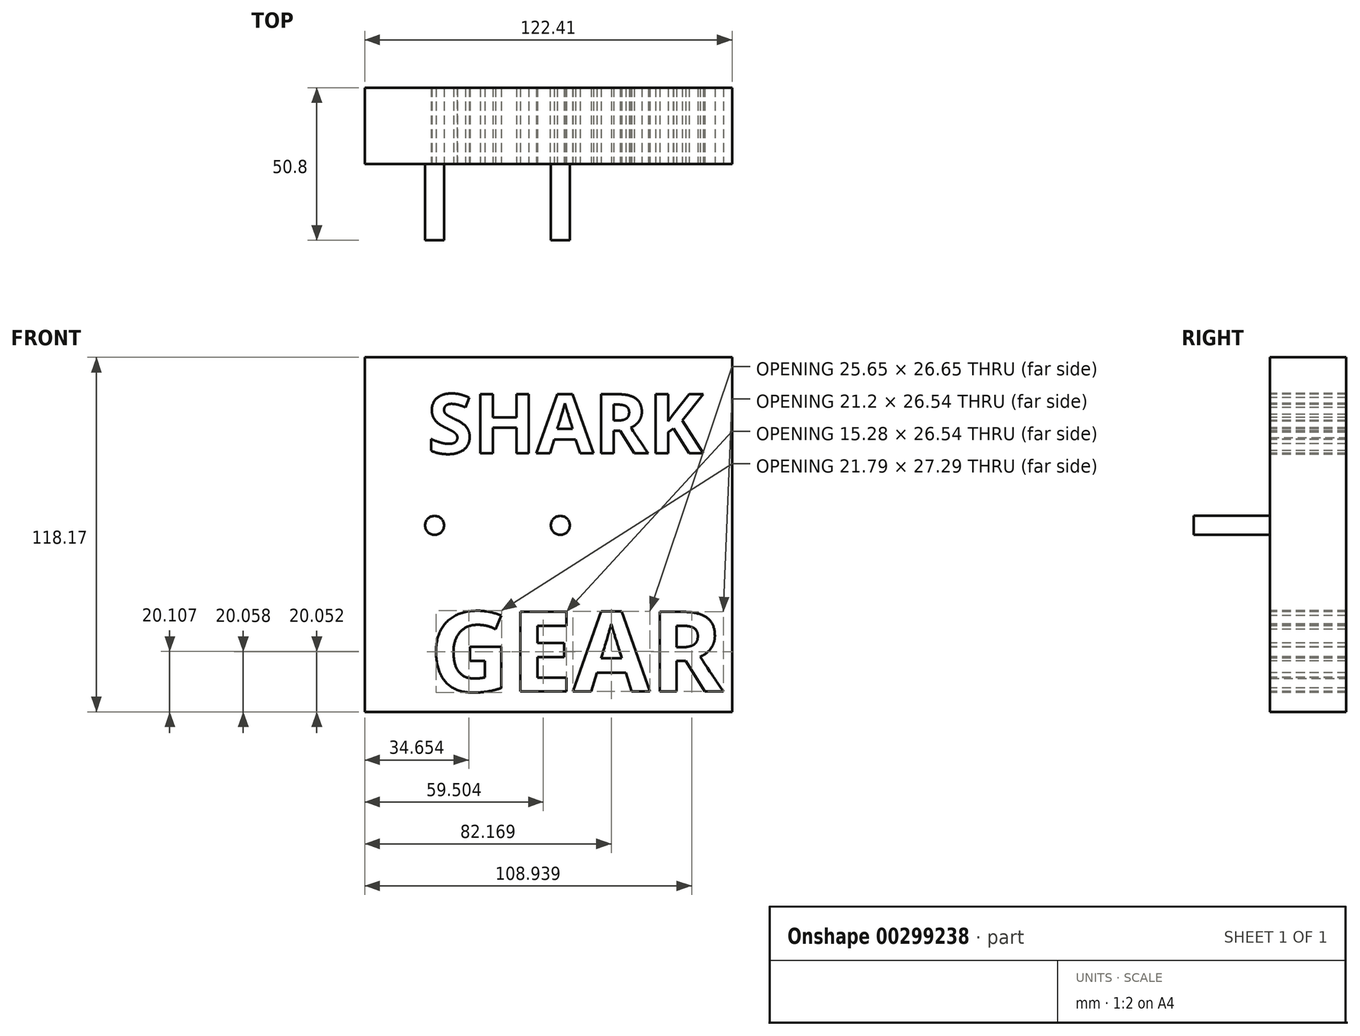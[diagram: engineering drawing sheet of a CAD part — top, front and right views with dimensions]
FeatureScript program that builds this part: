
annotation { "Feature Type Name" : "Feature", "Feature Type Description" : "" }
export const myFeature = defineFeature(function(context is Context, id is Id, definition is map)
    precondition{}
    {
        {
            var Q0;
            Q0=qCreatedBy(makeId("Front.planeOp"),FACE);
            var sketch = newSketch(context, id + "F0", { "sketchPlane" : qUnion([Q0])});
            skLineSegment(sketch, "E0.bottom", {"start": v(-56.78, 56.04) * mm, "end": v(65.63, 56.04) * mm});
            skLineSegment(sketch, "E0.top", {"start": v(-56.78, -62.13) * mm, "end": v(65.63, -62.13) * mm});
            skLineSegment(sketch, "E0.left", {"start": v(-56.78, 56.04) * mm, "end": v(-56.78, -62.13) * mm});
            skLineSegment(sketch, "E0.right", {"start": v(65.63, 56.04) * mm, "end": v(65.63, -62.13) * mm});
            skSolve(sketch);
        }
        {
            var Q0;
            Q0=makeQuery(id+"F0.imprint","IMPRINT",FACE,{"disambiguationData":[TD([[makeQuery(id+"F0.imprint","IMPRINT",EDGE,{"derivedFrom":sQuery(id+"F0.wireOp",EDGE,"E0.bottom")}),-1.0]])]});
            var sketch = newSketch(context, id + "F1", { "sketchPlane" : qUnion([Q0])});
            skCircle(sketch, "E1", {"center": v(-33.52, 0) * mm, "radius": 3.18 * mm});
            skCircle(sketch, "E2", {"center": v(8.4, 0) * mm, "radius": 3.18 * mm});
            skSolve(sketch);
        }
        {
            var Q0;
            Q0 = qSketchRegion(id + "F0", true);
            extrude(context, id + "F2", {"entities" : qUnion([Q0]), "depth" : 25.4 * mm});
        }
        {
            var Q0;
            Q0 = qSketchRegion(id + "F1", true);
            extrude(context, id + "F3", {"entities" : qUnion([Q0]), "operationType" : NewBodyOperationType.ADD, "depth" : 50.8 * mm});
        }
        {
            var Q0;
            Q0=makeQuery(id+"F2.opExtrude","CAP_FACE",FACE,{"disambiguationData":[OSD([sQuery(id+"F0.wireOp",EDGE,"E0.bottom"),sQuery(id+"F0.wireOp",EDGE,"E0.top"),sQuery(id+"F0.wireOp",EDGE,"E0.left"),sQuery(id+"F0.wireOp",EDGE,"E0.right")])],"isStart":false});
            var sketch = newSketch(context, id + "F4", { "sketchPlane" : qUnion([Q0])});
            skText(sketch, "E3", { "text": "SHARK", "fontName": "OpenSans-Bold.ttf"});
            skText(sketch, "E4", { "text": "GEAR", "fontName": "OpenSans-Bold.ttf"});
            const initialGuessF4  = {"E3": [-0.03594, 0.024, 1, 0, 0.01988], "E4": [-0.03518, -0.05535, 1, 0, 0.02677]};
            skSetInitialGuess(sketch, initialGuessF4);
            skSolve(sketch);
        }
        {
            var Q0;
            Q0 = qSketchRegion(id + "F4", true);
            extrude(context, id + "F5", {"entities" : qUnion([Q0]), "operationType" : NewBodyOperationType.REMOVE, "oppositeDirection" : true, "depth" : 25.4 * mm});
        }
    });
